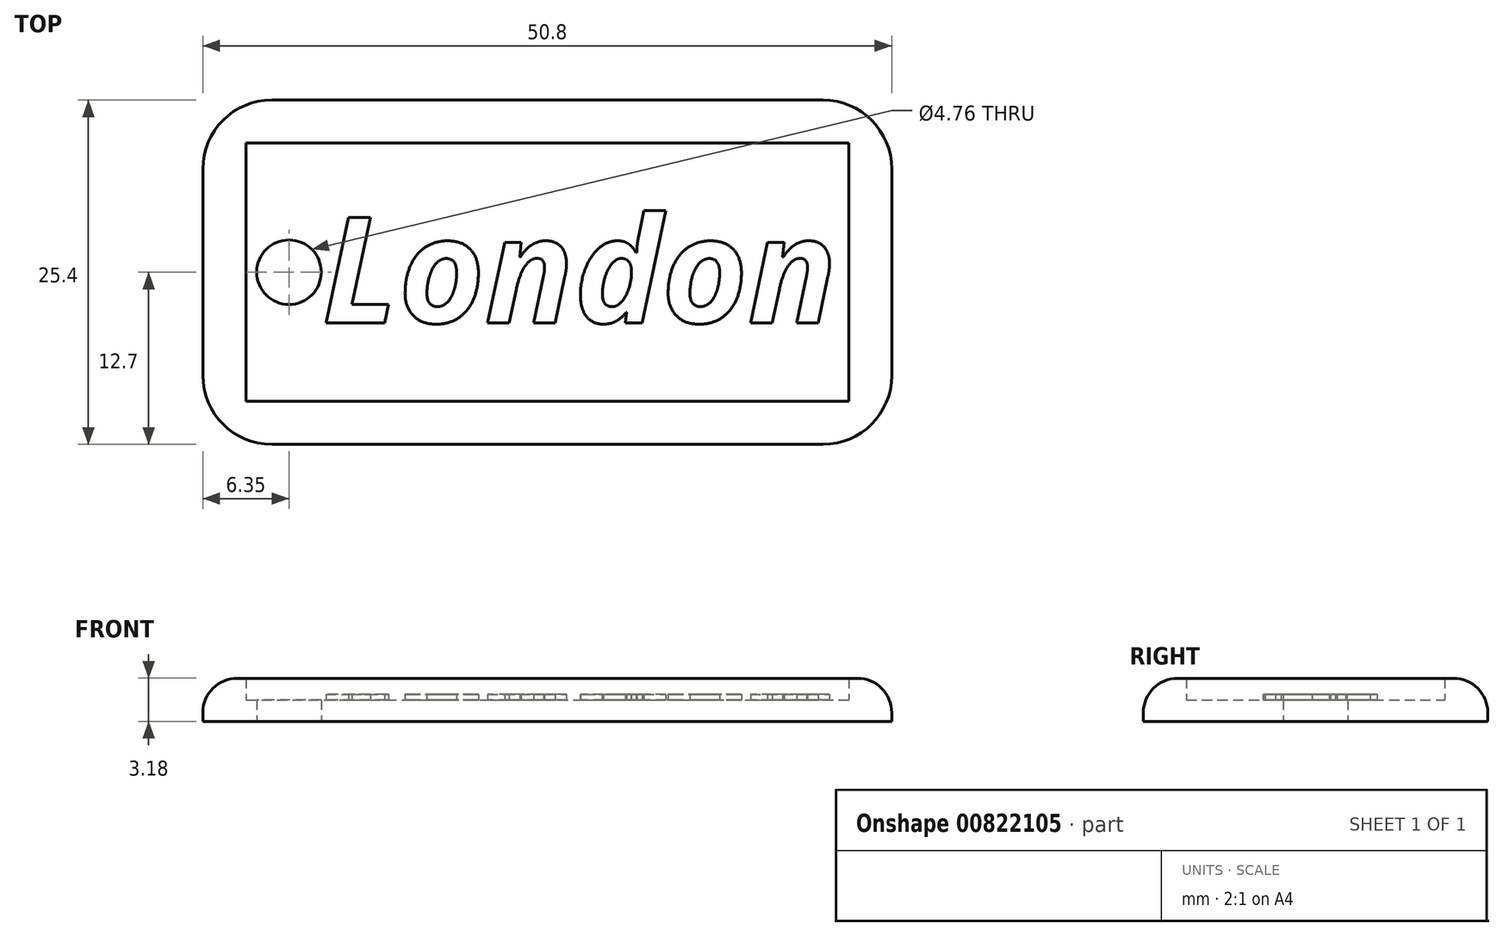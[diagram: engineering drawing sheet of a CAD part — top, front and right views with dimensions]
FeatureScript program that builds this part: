
annotation { "Feature Type Name" : "Feature", "Feature Type Description" : "" }
export const myFeature = defineFeature(function(context is Context, id is Id, definition is map)
    precondition{}
    {
        {
            var Q0;
            Q0=qCreatedBy(makeId("Top.planeOp"),FACE);
            var sketch = newSketch(context, id + "F0", { "sketchPlane" : qUnion([Q0])});
            skLineSegment(sketch, "E0.bottom", {"start": v(0, 0) * mm, "end": v(50.8, 0) * mm});
            skLineSegment(sketch, "E0.top", {"start": v(0, 25.4) * mm, "end": v(50.8, 25.4) * mm});
            skLineSegment(sketch, "E0.left", {"start": v(0, 0) * mm, "end": v(0, 25.4) * mm});
            skLineSegment(sketch, "E0.right", {"start": v(50.8, 0) * mm, "end": v(50.8, 25.4) * mm});
            skCircle(sketch, "E1", {"center": v(6.35, 12.7) * mm, "radius": 2.38 * mm});
            skPoint(sketch, "E1.centerSnap0", {"position": v(0, 12.7) * mm});
            skLineSegment(sketch, "E2.0", {"start": v(3.17, 22.23) * mm, "end": v(47.62, 22.23) * mm});
            skLineSegment(sketch, "E2.1", {"start": v(3.18, 3.18) * mm, "end": v(3.17, 22.22) * mm});
            skLineSegment(sketch, "E2.2", {"start": v(3.18, 3.18) * mm, "end": v(47.62, 3.18) * mm});
            skLineSegment(sketch, "E2.3", {"start": v(47.62, 3.18) * mm, "end": v(47.62, 22.23) * mm});
            skSolve(sketch);
        }
        {
            var Q0;
            Q0=makeQuery(id+"F0.imprint","IMPRINT",FACE,{"disambiguationData":[TD([[makeQuery(id+"F0.imprint","IMPRINT",EDGE,{"derivedFrom":sQuery(id+"F0.wireOp",EDGE,"E1")}),-1.0]])]});
            extrude(context, id + "F1", {"entities" : qUnion([Q0]), "depth" : 1.59 * mm, "offsetDistance" : 25.4 * mm});
        }
        {
            var Q0;
            Q0 = qSketchRegion(id + "F0", true);
            extrude(context, id + "F2", {"entities" : qUnion([Q0]), "operationType" : NewBodyOperationType.ADD, "depth" : 3.17 * mm, "offsetDistance" : 25.4 * mm});
        }
        {
            var Q0;
            Q0=makeQuery(id+"F2.opExtrude","SWEPT_EDGE",EDGE,{"disambiguationData":[OSD([sQuery(id+"F0.wireOp",EDGE,"E0.bottom"),sQuery(id+"F0.wireOp",EDGE,"E0.right")])]});
            var Q1;
            Q1=makeQuery(id+"F2.opExtrude","SWEPT_EDGE",EDGE,{"disambiguationData":[OSD([sQuery(id+"F0.wireOp",EDGE,"E0.bottom"),sQuery(id+"F0.wireOp",EDGE,"E0.left")])]});
            var Q2;
            Q2=makeQuery(id+"F2.opExtrude","SWEPT_EDGE",EDGE,{"disambiguationData":[OSD([sQuery(id+"F0.wireOp",EDGE,"E0.top"),sQuery(id+"F0.wireOp",EDGE,"E0.left")])]});
            var Q3;
            Q3=makeQuery(id+"F2.opExtrude","SWEPT_EDGE",EDGE,{"disambiguationData":[OSD([sQuery(id+"F0.wireOp",EDGE,"E0.top"),sQuery(id+"F0.wireOp",EDGE,"E0.right")])]});
            fillet(context, id + "F3", {"entities" : qUnion([Q0, Q1, Q2, Q3]), "radius" : 5.08 * mm, "tangentPropagation" : true, "allowEdgeOverflow" : false});
        }
        {
            var Q0;
            Q0=makeQuery(id+"F2.opExtrude","CAP_EDGE",EDGE,{"disambiguationData":[OSD([sQuery(id+"F0.wireOp",EDGE,"E0.top")])],"isStart":false});
            fillet(context, id + "F4", {"entities" : qUnion([Q0]), "radius" : 2.54 * mm, "tangentPropagation" : true, "allowEdgeOverflow" : false});
        }
        {
            var Q0;
            Q0=makeQuery(id+"F1.opExtrude","CAP_FACE",FACE,{"disambiguationData":[OSD([sQuery(id+"F0.wireOp",EDGE,"E1"),sQuery(id+"F0.wireOp",EDGE,"E2.0"),sQuery(id+"F0.wireOp",EDGE,"E2.1"),sQuery(id+"F0.wireOp",EDGE,"E2.2"),sQuery(id+"F0.wireOp",EDGE,"E2.3")])],"isStart":false});
            var sketch = newSketch(context, id + "F5", { "sketchPlane" : qUnion([Q0])});
            skText(sketch, "E3", { "text": "London", "fontName": "OpenSans-BoldItalic.ttf"});
            const initialGuessF5  = {"E3": [0.0088, 0.00897, 1, 0, 0.00783]};
            skSetInitialGuess(sketch, initialGuessF5);
            skSolve(sketch);
        }
        {
            var Q0;
            Q0 = qSketchRegion(id + "F5", true);
            extrude(context, id + "F6", {"entities" : qUnion([Q0]), "operationType" : NewBodyOperationType.ADD, "depth" : 0.4 * mm, "offsetDistance" : 25.4 * mm});
        }
    });
